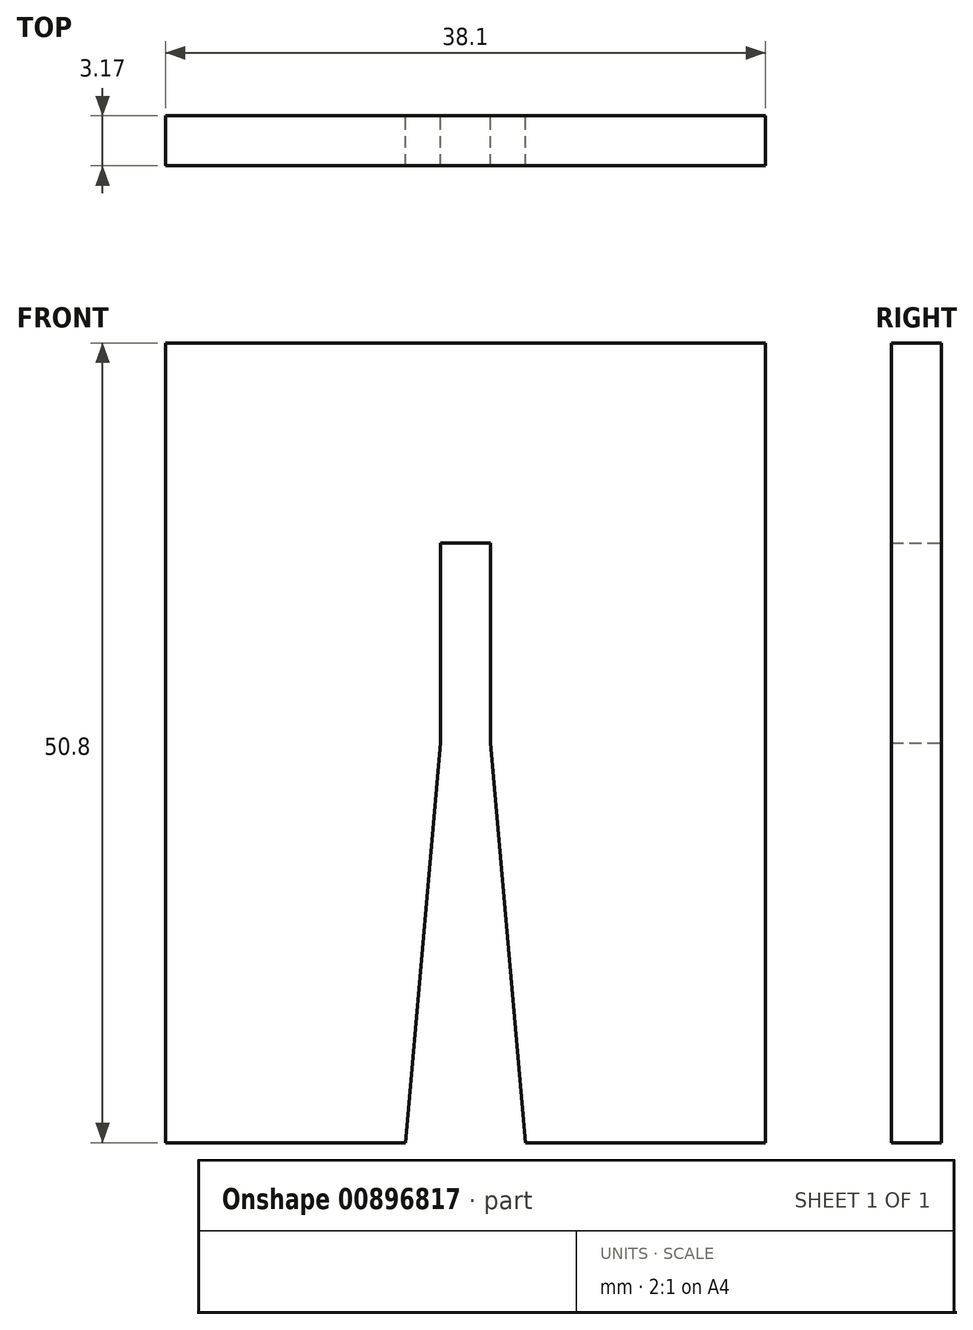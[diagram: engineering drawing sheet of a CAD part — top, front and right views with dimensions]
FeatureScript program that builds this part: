
annotation { "Feature Type Name" : "Feature", "Feature Type Description" : "" }
export const myFeature = defineFeature(function(context is Context, id is Id, definition is map)
    precondition{}
    {
        {
            var Q0;
            Q0=qCreatedBy(makeId("Front.planeOp"),FACE);
            var sketch = newSketch(context, id + "F0", { "sketchPlane" : qUnion([Q0])});
            skLineSegment(sketch, "E0.bottom", {"start": v(19.05, -25.4) * mm, "end": v(3.8, -25.4) * mm});
            skLineSegment(sketch, "E0.top", {"start": v(19.05, 25.4) * mm, "end": v(-19.05, 25.4) * mm});
            skLineSegment(sketch, "E0.left", {"start": v(19.05, -25.4) * mm, "end": v(19.05, 25.4) * mm});
            skLineSegment(sketch, "E0.right", {"start": v(-19.05, -25.4) * mm, "end": v(-19.05, 25.4) * mm});
            skPoint(sketch, "E0.middle", {"position": v(0, 0) * mm});
            skLineSegment(sketch, "E1", {"start": v(0, 0) * mm, "end": v(0, -25.4) * mm, "construction": true});
            skLineSegment(sketch, "E2.trimOffspring", {"start": v(-3.8, -25.4) * mm, "end": v(-19.05, -25.4) * mm});
            skLineSegment(sketch, "E3.top", {"start": v(-1.59, 12.7) * mm, "end": v(1.59, 12.7) * mm});
            skLineSegment(sketch, "E3.left", {"start": v(-1.59, 0) * mm, "end": v(-1.59, 12.7) * mm});
            skLineSegment(sketch, "E3.right", {"start": v(1.59, 0) * mm, "end": v(1.59, 12.7) * mm});
            skLineSegment(sketch, "E4", {"start": v(-1.59, 0) * mm, "end": v(-3.8, -25.4) * mm});
            skLineSegment(sketch, "E5", {"start": v(1.59, 0) * mm, "end": v(3.8, -25.4) * mm});
            skSolve(sketch);
        }
        {
            var Q0;
            Q0 = qSketchRegion(id + "F0", true);
            extrude(context, id + "F1", {"entities" : qUnion([Q0]), "depth" : 3.17 * mm, "offsetDistance" : 25.4 * mm});
        }
    });
